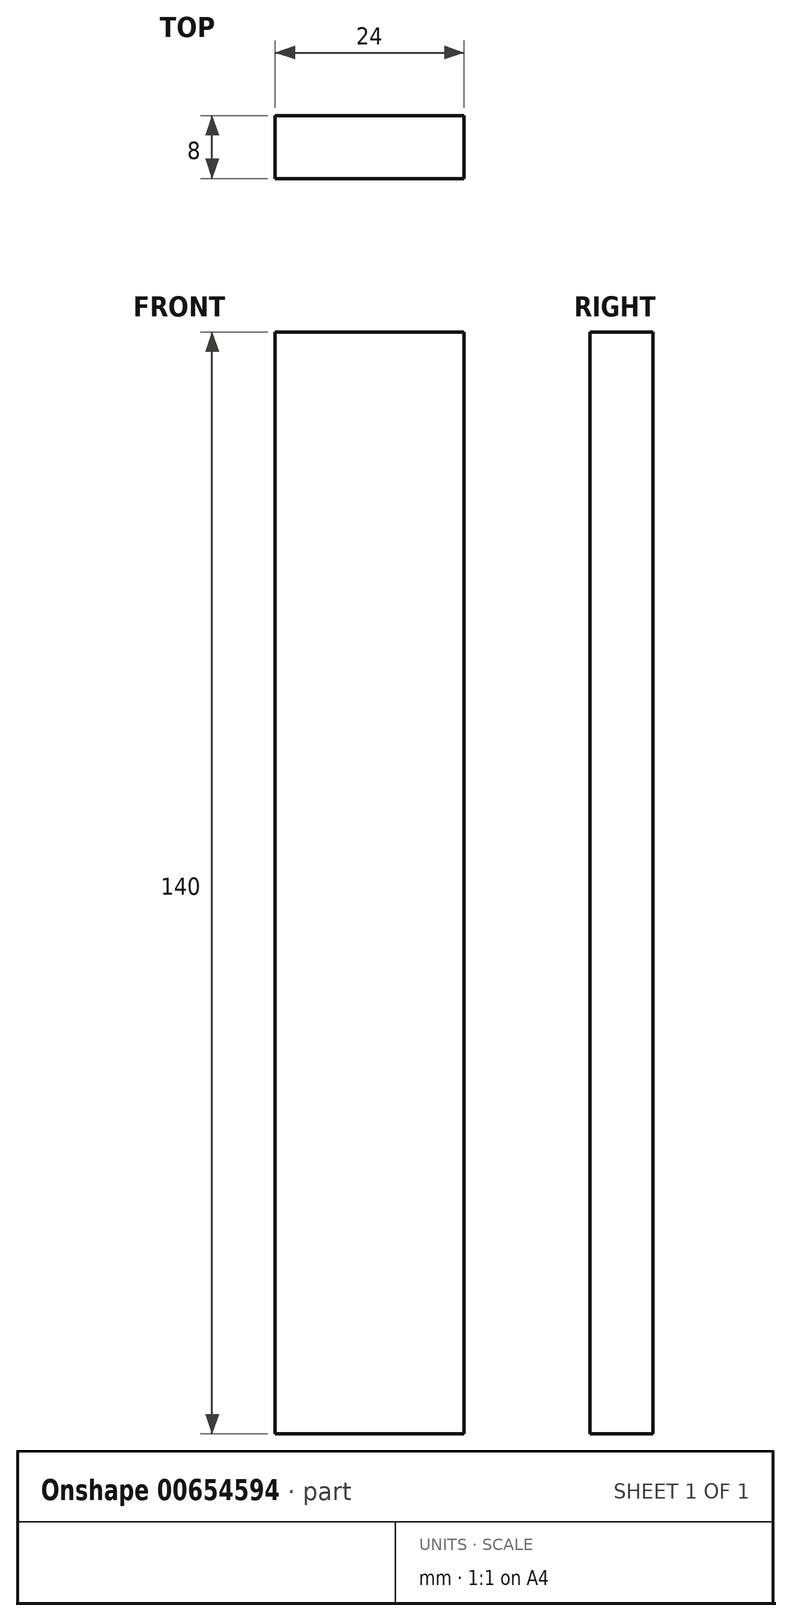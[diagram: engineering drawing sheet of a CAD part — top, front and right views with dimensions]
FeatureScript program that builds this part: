
annotation { "Feature Type Name" : "Feature", "Feature Type Description" : "" }
export const myFeature = defineFeature(function(context is Context, id is Id, definition is map)
    precondition{}
    {
        {
            var Q0;
            Q0=qCreatedBy(makeId("Front.planeOp"),FACE);
            var sketch = newSketch(context, id + "F0", { "sketchPlane" : qUnion([Q0])});
            skLineSegment(sketch, "E0.bottom", {"start": v(0, 0) * mm, "end": v(24, 0) * mm});
            skLineSegment(sketch, "E0.top", {"start": v(0, 140) * mm, "end": v(24, 140) * mm});
            skLineSegment(sketch, "E0.left", {"start": v(0, 0) * mm, "end": v(0, 140) * mm});
            skLineSegment(sketch, "E0.right", {"start": v(24, 0) * mm, "end": v(24, 140) * mm});
            skSolve(sketch);
        }
        {
            var Q0;
            Q0=makeQuery(id+"F0.imprint","IMPRINT",FACE,{"disambiguationData":[TD([[makeQuery(id+"F0.imprint","IMPRINT",EDGE,{"derivedFrom":sQuery(id+"F0.wireOp",EDGE,"E0.bottom")}),1.0]])]});
            extrude(context, id + "F1", {"entities" : qUnion([Q0]), "oppositeDirection" : true, "depth" : 8 * mm, "offsetDistance" : 25 * mm});
        }
    });
